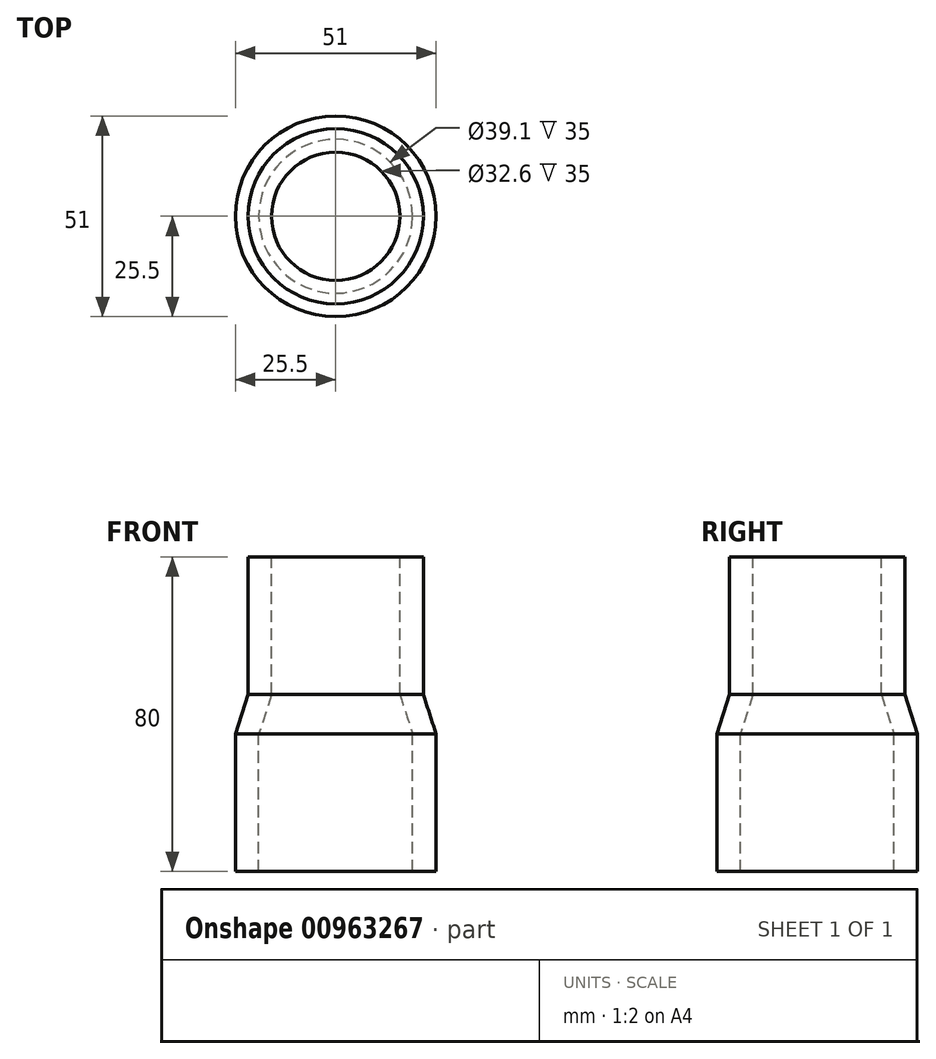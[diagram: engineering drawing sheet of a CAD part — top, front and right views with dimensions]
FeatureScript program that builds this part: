
annotation { "Feature Type Name" : "Feature", "Feature Type Description" : "" }
export const myFeature = defineFeature(function(context is Context, id is Id, definition is map)
    precondition{}
    {
        {
            var Q0;
            Q0=qCreatedBy(makeId("Front.planeOp"),FACE);
            var sketch = newSketch(context, id + "F0", { "sketchPlane" : qUnion([Q0])});
            skLineSegment(sketch, "E0", {"start": v(0, 68.2) * mm, "end": v(0, -71.8) * mm, "construction": true});
            skPoint(sketch, "E1", {"position": v(-16.3, 35) * mm});
            skPoint(sketch, "E2", {"position": v(-22.25, 35) * mm});
            skPoint(sketch, "E3", {"position": v(-16.3, 0) * mm});
            skPoint(sketch, "E4", {"position": v(-22.25, 0) * mm});
            skPoint(sketch, "E5", {"position": v(-19.55, -10) * mm});
            skPoint(sketch, "E6", {"position": v(-25.5, -10) * mm});
            skPoint(sketch, "E7", {"position": v(-19.55, -45) * mm});
            skPoint(sketch, "E8", {"position": v(-25.5, -45) * mm});
            skLineSegment(sketch, "E9", {"start": v(-22.25, 35) * mm, "end": v(-16.3, 35) * mm});
            skLineSegment(sketch, "E10", {"start": v(-16.3, 35) * mm, "end": v(-16.3, 0) * mm});
            skLineSegment(sketch, "E11", {"start": v(-16.3, 0) * mm, "end": v(-19.55, -10) * mm});
            skLineSegment(sketch, "E12", {"start": v(-19.55, -10) * mm, "end": v(-19.55, -45) * mm});
            skLineSegment(sketch, "E13", {"start": v(-19.55, -45) * mm, "end": v(-25.5, -45) * mm});
            skLineSegment(sketch, "E14", {"start": v(-25.5, -45) * mm, "end": v(-25.5, -10) * mm});
            skLineSegment(sketch, "E15", {"start": v(-25.5, -10) * mm, "end": v(-22.25, 0) * mm});
            skLineSegment(sketch, "E16", {"start": v(-22.25, 0) * mm, "end": v(-22.25, 35) * mm});
            skSolve(sketch);
        }
        {
            var Q0;
            Q0=makeQuery(id+"F0.imprint","IMPRINT",FACE,{"disambiguationData":[TD([[makeQuery(id+"F0.imprint","IMPRINT",EDGE,{"derivedFrom":sQuery(id+"F0.wireOp",EDGE,"E9")}),-1.0]])]});
            var Q1;
            Q1=sQuery(id+"F0.wireOp",EDGE,"E0");
            revolve(context, id + "F1", {"surfaceOperationType" : NewSurfaceOperationType.NEW, "entities" : qUnion([Q0]), "axis" : qUnion([Q1]), "revolveType" : RevolveType.FULL});
        }
    });
